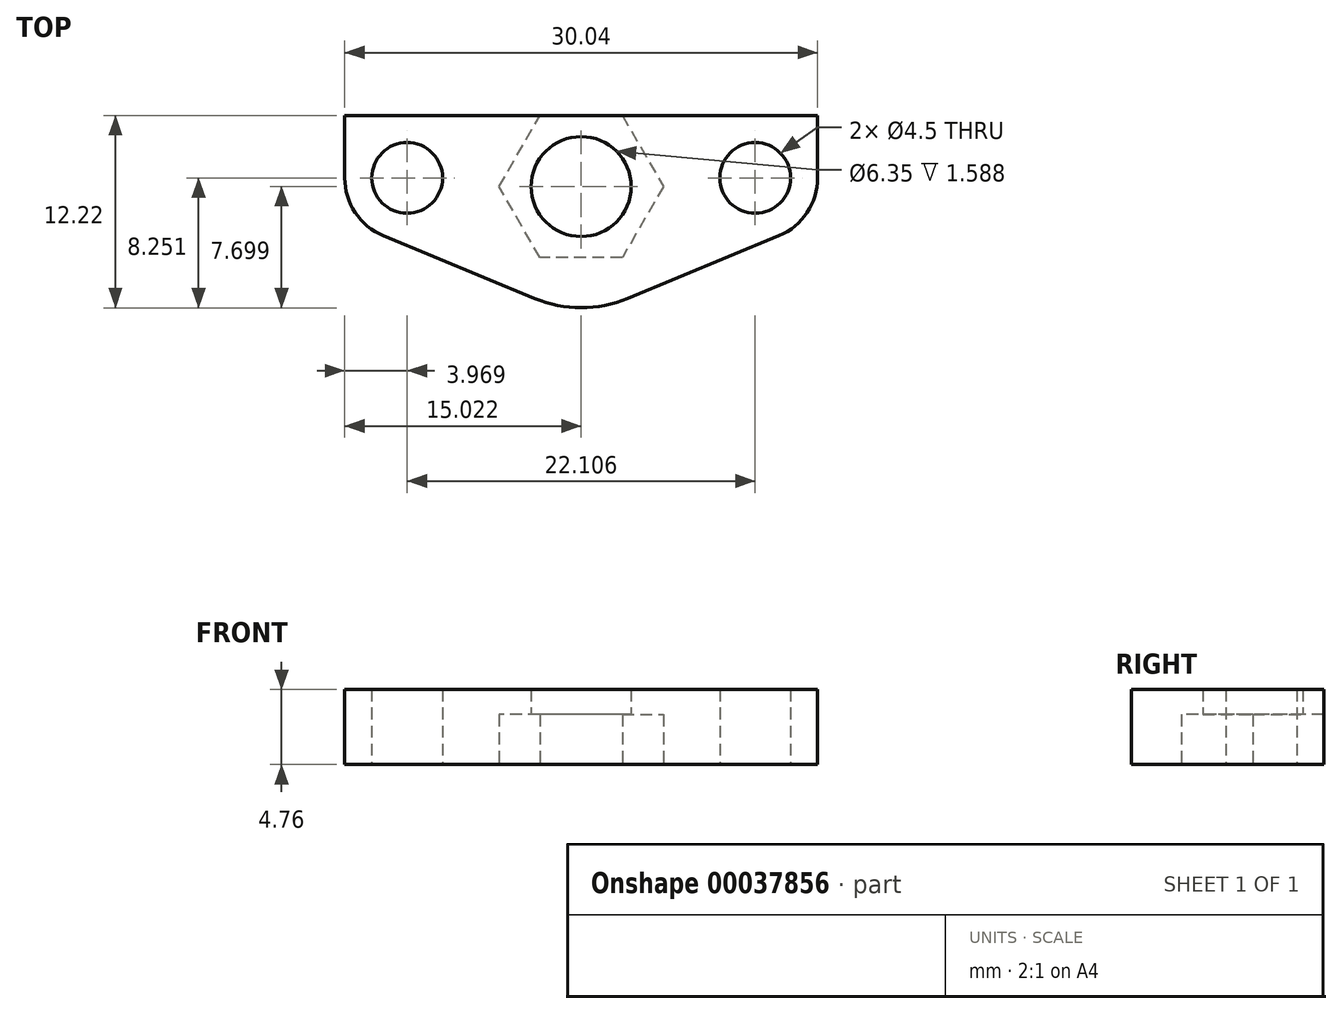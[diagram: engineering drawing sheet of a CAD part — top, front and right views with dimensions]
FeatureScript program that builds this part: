
annotation { "Feature Type Name" : "Feature", "Feature Type Description" : "" }
export const myFeature = defineFeature(function(context is Context, id is Id, definition is map)
    precondition{}
    {
        {
            var Q0;
            Q0=qCreatedBy(makeId("Top.planeOp"),FACE);
            var sketch = newSketch(context, id + "F0", { "sketchPlane" : qUnion([Q0])});
            skLineSegment(sketch, "E0", {"start": v(0, 0) * mm, "end": v(30.04, 0) * mm});
            skLineSegment(sketch, "E1", {"start": v(30.04, 0) * mm, "end": v(30.04, -3.97) * mm});
            skLineSegment(sketch, "E2", {"start": v(0, 0) * mm, "end": v(0, -3.97) * mm});
            skArc(sketch, "E3", {"start": v(0, -3.97) * mm, "mid": v(0.67, -6.17) * mm, "end": v(2.45, -7.63) * mm});
            skArc(sketch, "E4", {"start": v(27.6, -7.63) * mm, "mid": v(29.38, -6.17) * mm, "end": v(30.04, -3.97) * mm});
            skLineSegment(sketch, "E5", {"start": v(15.02, -4.52) * mm, "end": v(15.02, -12.22) * mm, "construction": true});
            skArc(sketch, "E6", {"start": v(12.07, -11.63) * mm, "mid": v(15.02, -12.22) * mm, "end": v(17.97, -11.63) * mm});
            skLineSegment(sketch, "E7", {"start": v(2.45, -7.63) * mm, "end": v(12.07, -11.63) * mm});
            skLineSegment(sketch, "E8", {"start": v(17.97, -11.63) * mm, "end": v(27.6, -7.63) * mm});
            skCircle(sketch, "E9.cCircle", {"center": v(15.02, -4.52) * mm, "radius": 4.52 * mm, "construction": true});
            skLineSegment(sketch, "E9.0", {"start": v(17.63, -9.04) * mm, "end": v(12.41, -9.04) * mm});
            skLineSegment(sketch, "E9.1", {"start": v(12.41, -9.04) * mm, "end": v(9.8, -4.52) * mm});
            skLineSegment(sketch, "E9.2", {"start": v(9.8, -4.52) * mm, "end": v(12.41, 0) * mm});
            skLineSegment(sketch, "E9.3", {"start": v(12.41, 0) * mm, "end": v(17.63, 0) * mm, "construction": true});
            skLineSegment(sketch, "E9.4", {"start": v(17.63, 0) * mm, "end": v(20.24, -4.52) * mm});
            skLineSegment(sketch, "E9.5", {"start": v(20.24, -4.52) * mm, "end": v(17.63, -9.04) * mm});
            skPoint(sketch, "E9.0.midPoint", {"position": v(15.02, -9.04) * mm});
            skCircle(sketch, "E10", {"center": v(3.97, -3.97) * mm, "radius": 2.25 * mm});
            skCircle(sketch, "E11", {"center": v(26.07, -3.97) * mm, "radius": 2.25 * mm});
            skSolve(sketch);
        }
        {
            var Q0;
            {var subQ3=sQuery(id+"F0.wireOp",EDGE,"E1");Q0=makeQuery(id+"F0.imprint","IMPRINT",FACE,{"disambiguationData":[TD([[makeQuery(id+"F0.imprint","IMPRINT",EDGE,{"derivedFrom":subQ3}),-1.0]])]});}
            extrude(context, id + "F1", {"entities" : qUnion([Q0]), "depth" : 3.17 * mm});
        }
        {
            var Q0;
            Q0=makeQuery(id+"F1.opExtrude","CAP_FACE",FACE,{"disambiguationData":[OSD([sQuery(id+"F0.wireOp",EDGE,"E0"),sQuery(id+"F0.wireOp",EDGE,"E1"),sQuery(id+"F0.wireOp",EDGE,"E2"),sQuery(id+"F0.wireOp",EDGE,"E3"),sQuery(id+"F0.wireOp",EDGE,"E4"),sQuery(id+"F0.wireOp",EDGE,"E6"),sQuery(id+"F0.wireOp",EDGE,"E7"),sQuery(id+"F0.wireOp",EDGE,"E8"),sQuery(id+"F0.wireOp",EDGE,"E9.0"),sQuery(id+"F0.wireOp",EDGE,"E9.1"),sQuery(id+"F0.wireOp",EDGE,"E9.2"),sQuery(id+"F0.wireOp",EDGE,"E9.3"),sQuery(id+"F0.wireOp",EDGE,"E9.4"),sQuery(id+"F0.wireOp",EDGE,"E9.5"),sQuery(id+"F0.wireOp",EDGE,"E10"),sQuery(id+"F0.wireOp",EDGE,"E11")])],"isStart":false});
            var sketch = newSketch(context, id + "F2", { "sketchPlane" : qUnion([Q0])});
            skCircle(sketch, "E12", {"center": v(15.02, -4.52) * mm, "radius": 3.18 * mm});
            skLineSegment(sketch, "E13", {"start": v(17.63, 0) * mm, "end": v(12.41, 0) * mm});
            skSolve(sketch);
        }
        {
            var Q0;
            Q0=makeQuery(id+"F2.imprint","IMPRINT",FACE,{"disambiguationData":[TD([[makeQuery(id+"F2.imprint","IMPRINT",EDGE,{"derivedFrom":sQuery(id+"F2.wireOp",EDGE,"E12")}),-1.0]])]});
            var Q1;
            Q1=makeQuery(id+"F2.imprint","IMPRINT",FACE,{"disambiguationData":[TD([[makeQuery(id+"F2.imprint","IMPRINT",EDGE,{"derivedFrom":makeQuery(id+"F1.opExtrude","CAP_EDGE",EDGE,{"disambiguationData":[OSD([sQuery(id+"F0.wireOp",EDGE,"E0")])],"isStart":false})}),-1.0]])]});
            extrude(context, id + "F3", {"entities" : qUnion([Q0, Q1]), "operationType" : NewBodyOperationType.ADD, "depth" : 1.59 * mm});
        }
    });
